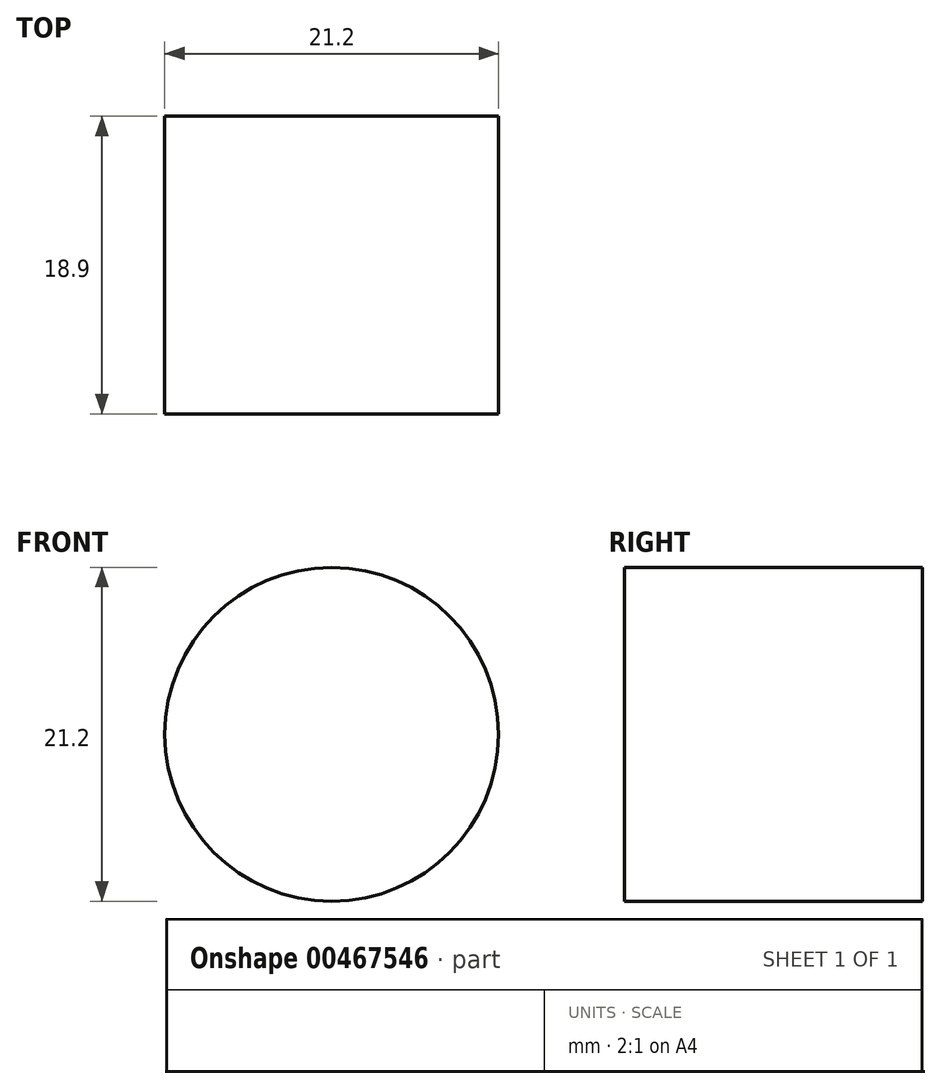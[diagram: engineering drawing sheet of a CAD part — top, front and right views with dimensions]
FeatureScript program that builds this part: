
annotation { "Feature Type Name" : "Feature", "Feature Type Description" : "" }
export const myFeature = defineFeature(function(context is Context, id is Id, definition is map)
    precondition{}
    {
        {
            var Q0;
            Q0=qCreatedBy(makeId("Front.planeOp"),FACE);
            var sketch = newSketch(context, id + "F0", { "sketchPlane" : qUnion([Q0])});
            skCircle(sketch, "E0", {"center": v(0, 0) * mm, "radius": 10.6 * mm});
            skSolve(sketch);
        }
        {
            var Q0;
            Q0 = qSketchRegion(id + "F0", true);
            extrude(context, id + "F1", {"entities" : qUnion([Q0]), "depth" : (9 * 2.1) * mm});
        }
    });
